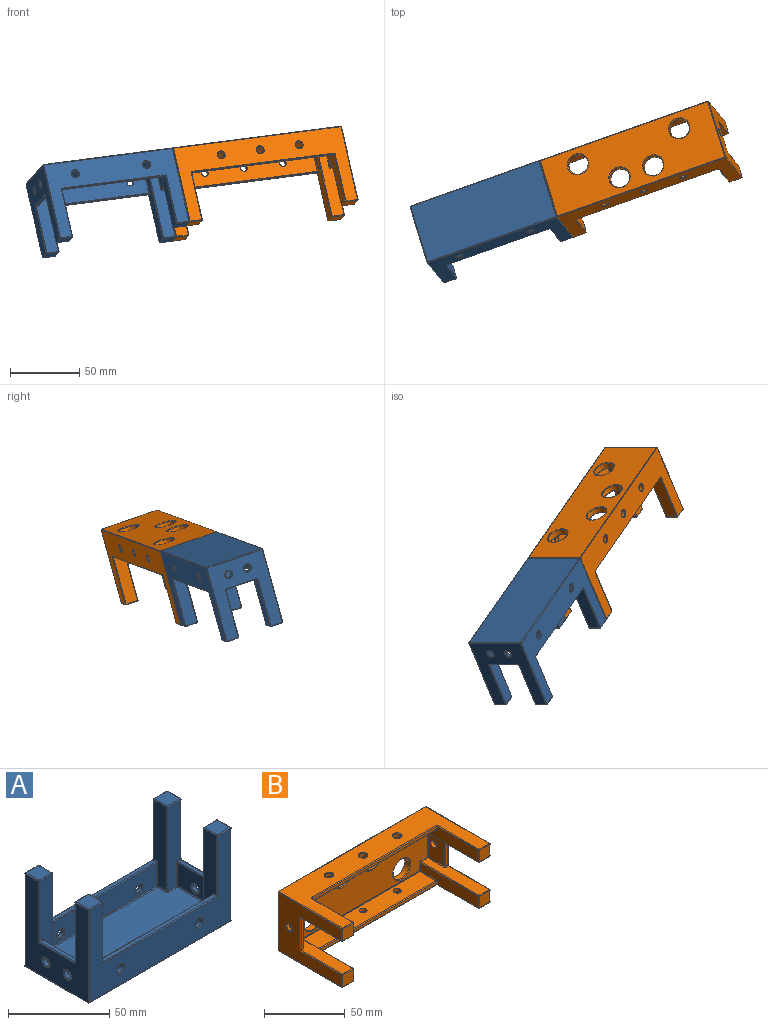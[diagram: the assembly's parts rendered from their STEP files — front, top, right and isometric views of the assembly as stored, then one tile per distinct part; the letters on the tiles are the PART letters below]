
ASSEMBLY  parts=2 mates=1
PART A: 165 faces, bbox 100x45x56.8 mm
  f0: plane 55.8x44mm, normal (1,0,0), area 1470.6mm2, adj f43,f115,f116,f127,f138,f139,f146,f151
  f1: plane 99x55.8mm, normal (0,1,0), area 2487.3mm2, adj f33,f35,f111,f134,f135,f143,f149,f150
  f2: plane 79x14mm, normal (0,-1,0), area 1049.5mm2, adj f34,f36,f108,f109,f131,f132
  f3: plane 99x55.8mm, normal (0,-1,0), area 2487.3mm2, adj f37,f38,f68,f77,f78,f86,f94,f95
  f4: plane 79x14mm, normal (0,1,0), area 1066.7mm2, adj f29,f30,f48,f54,f61,f62
  f5: plane 55.8x44mm, normal (-1,0,0), area 1442.3mm2, adj f39,f41,f66,f73,f74,f83,f92,f93
  f6: plane 24x14mm, normal (1,0,0), area 279.5mm2, adj f40,f42,f45,f55,f56,f57
  f7: plane 9x9mm, normal (0,0,1), area 81mm2, adj f96,f97,f114,f115
  f8: plane 9x9mm, normal (0,0,1), area 81mm2, adj f91,f110,f111,f112
  f9: plane 9x9mm, normal (0,0,1), area 81mm2, adj f153,f158,f161,f164
  f10: plane 9x9mm, normal (0,0,1), area 81mm2, adj f75,f76,f93,f94
  f11: plane 99x44mm, normal (0,0,-1), area 4356mm2, adj f136,f137,f150,f151
  f12: plane 50.8x9mm, normal (0,-1,0), area 412.4mm2, adj f56,f65,f71,f72,f90,f91,f92
  f13: plane 50.8x9mm, normal (0,1,0), area 412.4mm2, adj f45,f46,f51,f58,f59,f74,f75
  f14: plane 50.8x9mm, normal (1,0,0), area 412.4mm2, adj f47,f48,f53,f59,f60,f76,f77
  f15: plane 50.8x9mm, normal (-1,0,0), area 412.4mm2, adj f62,f69,f70,f79,f80,f95,f96
  f16: plane 50.8x9mm, normal (0,1,0), area 412.4mm2, adj f80,f88,f97,f98,f106,f116,f117
  f17: plane 24x14mm, normal (-1,0,0), area 307.7mm2, adj f44,f98,f107,f118,f119
  f18: plane 50.8x9mm, normal (0,-1,0), area 412.4mm2, adj f119,f128,f129,f140,f147,f152,f153
  f19: plane 50.8x9mm, normal (-1,0,0), area 412.4mm2, adj f130,f131,f142,f147,f148,f158,f159
  f20: plane 50.8x9mm, normal (1,0,0), area 412.4mm2, adj f89,f90,f109,f110,f122,f133,f134
  f21: plane 93x38mm, normal (0,0,1), area 3338.9mm2, adj f46,f47,f52,f54,f55,f70,f71,f81
  f22: plane 24x2mm, normal (0,0,1), area 48mm2, adj f117,f118,f139,f140
  f23: plane 79x2mm, normal (0,0,1), area 158mm2, adj f60,f61,f78,f79
  f24: plane 24x2mm, normal (0,0,1), area 48mm2, adj f57,f58,f72,f73
  f25: plane 79x2mm, normal (0,0,1), area 158mm2, adj f132,f133,f148,f149
  f26: cylinder r=2.5mm len=5mm, axis (1,0,0), area 31.4mm2, adj f43,f44
  f27: cylinder r=2.5mm len=5mm, axis (-1,0,0), area 31.4mm2, adj f39,f40
  f28: cylinder r=2.5mm len=5mm, axis (-1,0,0), area 31.4mm2, adj f41,f42
  f29: cylinder r=2.5mm len=5mm, axis (0,-1,0), area 39.3mm2, adj f4,f37
  f30: cylinder r=2.5mm len=5mm, axis (0,-1,0), area 39.3mm2, adj f4,f38
  f31: cylinder r=2.5mm len=5mm, axis (0,1,0), area 31.4mm2, adj f33,f34
  f32: cylinder r=2.5mm len=5mm, axis (0,1,0), area 31.4mm2, adj f35,f36
  f33: torus R=3mm, axis (0,1,0), area 13.2mm2, adj f1,f31
  f34: torus R=3mm, axis (0,-1,0), area 13.2mm2, adj f2,f31
  f35: torus R=3mm, axis (0,1,0), area 13.2mm2, adj f1,f32
  f36: torus R=3mm, axis (0,-1,0), area 13.2mm2, adj f2,f32
  f37: torus R=3mm, axis (0,1,0), area 13.2mm2, adj f3,f29
  f38: torus R=3mm, axis (0,1,0), area 13.2mm2, adj f3,f30
  f39: torus R=3mm, axis (1,0,0), area 13.2mm2, adj f5,f27
  f40: torus R=3mm, axis (-1,0,0), area 13.2mm2, adj f6,f27
  f41: torus R=3mm, axis (1,0,0), area 13.2mm2, adj f5,f28
  f42: torus R=3mm, axis (-1,0,0), area 13.2mm2, adj f6,f28
  f43: torus R=3mm, axis (1,0,0), area 13.2mm2, adj f0,f26
  f44: torus R=3mm, axis (-1,0,0), area 13.2mm2, adj f17,f26
  f45: cylinder r=0.5mm len=14mm, axis (0,0,-1), area 11mm2, adj f6,f13,f50,f51
  f46: cylinder r=0.5mm len=6mm, axis (1,0,0), area 4.7mm2, adj f13,f21,f50,f52
  f47: cylinder r=0.5mm len=6mm, axis (0,-1,0), area 4.7mm2, adj f14,f21,f49,f52
  f48: cylinder r=0.5mm len=14mm, axis (0,0,1), area 11mm2, adj f4,f14,f49,f53
  f49: sphere r=0.5mm, area 0.4mm2, adj f47,f48,f54
  f50: sphere r=0.5mm, area 0.4mm2, adj f45,f46,f55
  f51: torus R=1mm, axis (0,-1,0), area 0.8mm2, adj f13,f45,f57,f58
  f52: torus R=1mm, axis (0,0,1), area 0.8mm2, adj f21,f46,f47,f59
  f53: torus R=1mm, axis (1,0,0), area 0.8mm2, adj f14,f48,f60,f61
  f54: cylinder r=0.5mm len=79mm, axis (1,0,0), area 62mm2, adj f4,f21,f49,f63
  f55: cylinder r=0.5mm len=24mm, axis (0,-1,0), area 18.8mm2, adj f6,f21,f50,f64
  f56: cylinder r=0.5mm len=14mm, axis (0,0,1), area 11mm2, adj f6,f12,f64,f65
  f57: cylinder r=0.5mm len=24mm, axis (0,1,0), area 18.8mm2, adj f6,f24,f51,f65
  f58: cylinder r=0.5mm len=2mm, axis (1,0,0), area 1.6mm2, adj f13,f24,f51,f66
  f59: cylinder r=0.5mm len=50.8mm, axis (0,0,-1), area 39.9mm2, adj f13,f14,f52,f67
  f60: cylinder r=0.5mm len=2mm, axis (0,1,0), area 1.6mm2, adj f14,f23,f53,f68
  f61: cylinder r=0.5mm len=79mm, axis (-1,0,0), area 62mm2, adj f4,f23,f53,f69
  f62: cylinder r=0.5mm len=14mm, axis (0,0,-1), area 11mm2, adj f4,f15,f63,f69
  f63: sphere r=0.5mm, area 0.4mm2, adj f54,f62,f70
  f64: sphere r=0.5mm, area 0.4mm2, adj f55,f56,f71
  f65: torus R=1mm, axis (0,-1,0), area 0.8mm2, adj f12,f56,f57,f72
  f66: torus R=1mm, axis (1,0,0), area 0.8mm2, adj f5,f58,f73,f74
  f67: sphere r=0.5mm, area 0.4mm2, adj f59,f75,f76
  f68: torus R=1mm, axis (0,1,0), area 0.8mm2, adj f3,f60,f77,f78
  f69: torus R=1mm, axis (1,0,0), area 0.8mm2, adj f15,f61,f62,f79
  f70: cylinder r=0.5mm len=6mm, axis (0,1,0), area 4.7mm2, adj f15,f21,f63,f81
  f71: cylinder r=0.5mm len=6mm, axis (-1,0,0), area 4.7mm2, adj f12,f21,f64,f82
  f72: cylinder r=0.5mm len=2mm, axis (-1,0,0), area 1.6mm2, adj f12,f24,f65,f83
  f73: cylinder r=0.5mm len=24mm, axis (0,1,0), area 18.8mm2, adj f5,f24,f66,f83
  f74: cylinder r=0.5mm len=35.8mm, axis (0,0,1), area 28.1mm2, adj f5,f13,f66,f84
  f75: cylinder r=0.5mm len=9mm, axis (-1,0,0), area 7.1mm2, adj f10,f13,f67,f84
  f76: cylinder r=0.5mm len=9mm, axis (0,1,0), area 7.1mm2, adj f10,f14,f67,f85
  f77: cylinder r=0.5mm len=35.8mm, axis (0,0,-1), area 28.1mm2, adj f3,f14,f68,f85
  f78: cylinder r=0.5mm len=79mm, axis (-1,0,0), area 62mm2, adj f3,f23,f68,f86
  f79: cylinder r=0.5mm len=2mm, axis (0,-1,0), area 1.6mm2, adj f15,f23,f69,f86
  f80: cylinder r=0.5mm len=50.8mm, axis (0,0,-1), area 39.9mm2, adj f15,f16,f81,f87
  f81: torus R=1mm, axis (0,0,1), area 0.8mm2, adj f21,f70,f80,f88
  f82: torus R=1mm, axis (0,0,1), area 0.8mm2, adj f21,f71,f89,f90
  f83: torus R=1mm, axis (1,0,0), area 0.8mm2, adj f5,f72,f73,f92
  f84: sphere r=0.5mm, area 0.4mm2, adj f74,f75,f93
  f85: sphere r=0.5mm, area 0.4mm2, adj f76,f77,f94
  f86: torus R=1mm, axis (0,1,0), area 0.8mm2, adj f3,f78,f79,f95
  f87: sphere r=0.5mm, area 0.4mm2, adj f80,f96,f97
  f88: cylinder r=0.5mm len=6mm, axis (1,0,0), area 4.7mm2, adj f16,f21,f81,f99
  f89: cylinder r=0.5mm len=6mm, axis (0,-1,0), area 4.7mm2, adj f20,f21,f82,f100
  f90: cylinder r=0.5mm len=50.8mm, axis (0,0,-1), area 39.9mm2, adj f12,f20,f82,f101
  f91: cylinder r=0.5mm len=9mm, axis (1,0,0), area 7.1mm2, adj f8,f12,f101,f102
  f92: cylinder r=0.5mm len=35.8mm, axis (0,0,-1), area 28.1mm2, adj f5,f12,f83,f102
  f93: cylinder r=0.5mm len=9mm, axis (0,1,0), area 7.1mm2, adj f5,f10,f84,f103
  f94: cylinder r=0.5mm len=9mm, axis (-1,0,0), area 7.1mm2, adj f3,f10,f85,f103
  f95: cylinder r=0.5mm len=35.8mm, axis (0,0,1), area 28.1mm2, adj f3,f15,f86,f104
  f96: cylinder r=0.5mm len=9mm, axis (0,-1,0), area 7.1mm2, adj f7,f15,f87,f104
  f97: cylinder r=0.5mm len=9mm, axis (-1,0,0), area 7.1mm2, adj f7,f16,f87,f105
  f98: cylinder r=0.5mm len=14mm, axis (0,0,-1), area 11mm2, adj f16,f17,f99,f106
  f99: sphere r=0.5mm, area 0.4mm2, adj f88,f98,f107
  f100: sphere r=0.5mm, area 0.4mm2, adj f89,f108,f109
  f101: sphere r=0.5mm, area 0.4mm2, adj f90,f91,f110
  f102: sphere r=0.5mm, area 0.4mm2, adj f91,f92,f112
  f103: sphere r=0.5mm, area 0.4mm2, adj f93,f94,f113
  f104: sphere r=0.5mm, area 0.4mm2, adj f95,f96,f114
  f105: sphere r=0.5mm, area 0.4mm2, adj f97,f115,f116
  f106: torus R=1mm, axis (0,1,0), area 0.8mm2, adj f16,f98,f117,f118
  f107: cylinder r=0.5mm len=24mm, axis (0,1,0), area 18.8mm2, adj f17,f21,f99,f120
  f108: cylinder r=0.5mm len=79mm, axis (-1,0,0), area 62mm2, adj f2,f21,f100,f121
  f109: cylinder r=0.5mm len=14mm, axis (0,0,1), area 11mm2, adj f2,f20,f100,f122
  f110: cylinder r=0.5mm len=9mm, axis (0,1,0), area 7.1mm2, adj f8,f20,f101,f123
  f111: cylinder r=0.5mm len=9mm, axis (1,0,0), area 7.1mm2, adj f1,f8,f123,f124
  f112: cylinder r=0.5mm len=9mm, axis (0,1,0), area 7.1mm2, adj f5,f8,f102,f124
  f113: cylinder r=0.5mm len=55.8mm, axis (0,0,-1), area 43.8mm2, adj f3,f5,f103,f125
  f114: cylinder r=0.5mm len=9mm, axis (-1,0,0), area 7.1mm2, adj f3,f7,f104,f126
  f115: cylinder r=0.5mm len=9mm, axis (0,-1,0), area 7.1mm2, adj f0,f7,f105,f126
  f116: cylinder r=0.5mm len=35.8mm, axis (0,0,1), area 28.1mm2, adj f0,f16,f105,f127
  f117: cylinder r=0.5mm len=2mm, axis (1,0,0), area 1.6mm2, adj f16,f22,f106,f127
  f118: cylinder r=0.5mm len=24mm, axis (0,-1,0), area 18.8mm2, adj f17,f22,f106,f128
  f119: cylinder r=0.5mm len=14mm, axis (0,0,1), area 11mm2, adj f17,f18,f120,f128
  f120: sphere r=0.5mm, area 0.4mm2, adj f107,f119,f129
  f121: sphere r=0.5mm, area 0.4mm2, adj f108,f130,f131
  f122: torus R=1mm, axis (-1,0,0), area 0.8mm2, adj f20,f109,f132,f133
  f123: sphere r=0.5mm, area 0.4mm2, adj f110,f111,f134
  f124: sphere r=0.5mm, area 0.4mm2, adj f111,f112,f135
  f125: sphere r=0.5mm, area 0.4mm2, adj f113,f136,f137
  f126: sphere r=0.5mm, area 0.4mm2, adj f114,f115,f138
  f127: torus R=1mm, axis (1,0,0), area 0.8mm2, adj f0,f116,f117,f139
  f128: torus R=1mm, axis (0,1,0), area 0.8mm2, adj f18,f118,f119,f140
  f129: cylinder r=0.5mm len=6mm, axis (-1,0,0), area 4.7mm2, adj f18,f21,f120,f141
  f130: cylinder r=0.5mm len=6mm, axis (0,1,0), area 4.7mm2, adj f19,f21,f121,f141
  f131: cylinder r=0.5mm len=14mm, axis (0,0,-1), area 11mm2, adj f2,f19,f121,f142
  f132: cylinder r=0.5mm len=79mm, axis (1,0,0), area 62mm2, adj f2,f25,f122,f142
  f133: cylinder r=0.5mm len=2mm, axis (0,1,0), area 1.6mm2, adj f20,f25,f122,f143
  f134: cylinder r=0.5mm len=35.8mm, axis (0,0,-1), area 28.1mm2, adj f1,f20,f123,f143
  f135: cylinder r=0.5mm len=55.8mm, axis (0,0,1), area 43.8mm2, adj f1,f5,f124,f144
  f136: cylinder r=0.5mm len=44mm, axis (0,-1,0), area 34.6mm2, adj f5,f11,f125,f144
  f137: cylinder r=0.5mm len=99mm, axis (1,0,0), area 77.8mm2, adj f3,f11,f125,f145
  f138: cylinder r=0.5mm len=55.8mm, axis (0,0,1), area 43.8mm2, adj f0,f3,f126,f145
  f139: cylinder r=0.5mm len=24mm, axis (0,-1,0), area 18.8mm2, adj f0,f22,f127,f146
  f140: cylinder r=0.5mm len=2mm, axis (-1,0,0), area 1.6mm2, adj f18,f22,f128,f146
  f141: torus R=1mm, axis (0,0,1), area 0.8mm2, adj f21,f129,f130,f147
  f142: torus R=1mm, axis (-1,0,0), area 0.8mm2, adj f19,f131,f132,f148
  f143: torus R=1mm, axis (0,1,0), area 0.8mm2, adj f1,f133,f134,f149
  f144: sphere r=0.5mm, area 0.4mm2, adj f135,f136,f150
  f145: sphere r=0.5mm, area 0.4mm2, adj f137,f138,f151
  f146: torus R=1mm, axis (1,0,0), area 0.8mm2, adj f0,f139,f140,f152
  f147: cylinder r=0.5mm len=50.8mm, axis (0,0,-1), area 39.9mm2, adj f18,f19,f141,f154
  f148: cylinder r=0.5mm len=2mm, axis (0,-1,0), area 1.6mm2, adj f19,f25,f142,f155
  f149: cylinder r=0.5mm len=79mm, axis (1,0,0), area 62mm2, adj f1,f25,f143,f155
  f150: cylinder r=0.5mm len=99mm, axis (-1,0,0), area 77.8mm2, adj f1,f11,f144,f156
  f151: cylinder r=0.5mm len=44mm, axis (0,1,0), area 34.6mm2, adj f0,f11,f145,f156
  f152: cylinder r=0.5mm len=35.8mm, axis (0,0,-1), area 28.1mm2, adj f0,f18,f146,f157
  f153: cylinder r=0.5mm len=9mm, axis (1,0,0), area 7.1mm2, adj f9,f18,f154,f157
  f154: sphere r=0.5mm, area 0.4mm2, adj f147,f153,f158
  f155: torus R=1mm, axis (0,1,0), area 0.8mm2, adj f1,f148,f149,f159
  f156: sphere r=0.5mm, area 0.4mm2, adj f150,f151,f160
  f157: sphere r=0.5mm, area 0.4mm2, adj f152,f153,f161
  f158: cylinder r=0.5mm len=9mm, axis (0,-1,0), area 7.1mm2, adj f9,f19,f154,f162
  f159: cylinder r=0.5mm len=35.8mm, axis (0,0,1), area 28.1mm2, adj f1,f19,f155,f162
  f160: cylinder r=0.5mm len=55.8mm, axis (0,0,-1), area 43.8mm2, adj f0,f1,f156,f163
  f161: cylinder r=0.5mm len=9mm, axis (0,-1,0), area 7.1mm2, adj f0,f9,f157,f163
  f162: sphere r=0.5mm, area 0.4mm2, adj f158,f159,f164
  f163: sphere r=0.5mm, area 0.4mm2, adj f160,f161,f164
  f164: cylinder r=0.5mm len=9mm, axis (1,0,0), area 7.1mm2, adj f1,f9,f162,f163
PART B: 165 faces, bbox 130x56.8x45 mm
  f0: plane 50.8x9mm, normal (1,0,0), area 412.4mm2, adj f63,f64,f74,f85,f86,f104,f105
  f1: plane 50.8x9mm, normal (0,0,1), area 412.4mm2, adj f45,f46,f58,f59,f71,f82,f83
  f2: plane 129x55.8mm, normal (0,0,-1), area 3029mm2, adj f38,f39,f43,f49,f50,f54,f64,f65
  f3: plane 50.8x9mm, normal (0,0,1), area 421mm2, adj f22,f23,f87,f88,f105,f119,f164
  f4: plane 123x38mm, normal (0,-1,0), area 3694.6mm2, adj f60,f72,f83,f84,f103,f104,f113,f118
  f5: plane 50.8x9mm, normal (-1,0,0), area 412.4mm2, adj f110,f117,f123,f129,f134,f135,f139
  f6: plane 55.8x44mm, normal (-1,0,0), area 1470.1mm2, adj f66,f67,f88,f89,f98,f106,f107,f108
  f7: plane 109x2mm, normal (0,-1,0), area 218mm2, adj f133,f134,f142,f143
  f8: plane 109x2mm, normal (0,-1,0), area 218mm2, adj f48,f49,f62,f63
  f9: plane 9x9mm, normal (0,-1,0), area 81mm2, adj f65,f66,f86,f87
  f10: plane 9x9mm, normal (0,-1,0), area 81mm2, adj f39,f40,f46,f47
  f11: plane 55.8x44mm, normal (1,0,0), area 1470.6mm2, adj f40,f45,f50,f51,f57,f69,f70,f79
  f12: plane 9x9mm, normal (0,-1,0), area 81mm2, adj f107,f120,f121,f122
  f13: plane 129x55.8mm, normal (0,0,1), area 3029mm2, adj f90,f91,f108,f109,f122,f123,f128,f132
  f14: plane 9x9mm, normal (0,-1,0), area 81mm2, adj f92,f101,f109,f110
  f15: plane 129x44mm, normal (0,1,0), area 4891.7mm2, adj f68,f69,f89,f90,f156,f158,f160,f162
  f16: plane 50.8x9mm, normal (1,0,0), area 412.4mm2, adj f121,f131,f132,f141,f142,f145,f146
  f17: plane 50.8x9mm, normal (-1,0,0), area 412.4mm2, adj f38,f47,f48,f53,f59,f60,f61
  f18: plane 50.8x9mm, normal (0,0,-1), area 412.4mm2, adj f79,f80,f94,f101,f102,f117,f118
  f19: plane 50.8x9mm, normal (0,0,-1), area 421mm2, adj f22,f23,f106,f120,f130,f131,f164
  f20: plane 109x14mm, normal (0,0,-1), area 1467.1mm2, adj f30,f31,f32,f135,f140,f143,f146
  f21: plane 109x14mm, normal (0,0,1), area 1467.1mm2, adj f34,f35,f36,f61,f62,f84,f85
  f22: plane 25x14mm, normal (1,0,0), area 321.7mm2, adj f3,f19,f125,f148,f164
  f23: plane 25x2mm, normal (0,-1,0), area 50mm2, adj f3,f19,f98,f164
  f24: plane 24x14mm, normal (-1,0,0), area 316.4mm2, adj f33,f81,f82,f102,f103
  f25: plane 24x2mm, normal (0,-1,0), area 48mm2, adj f57,f58,f80,f81
  f26: cylinder r=7.4mm len=14.8mm, axis (0,1,0), area 186mm2, adj f156,f157
  f27: cylinder r=7.4mm len=14.8mm, axis (0,1,0), area 186mm2, adj f158,f159
  f28: cylinder r=7.4mm len=14.8mm, axis (0,1,0), area 186mm2, adj f160,f161
  f29: cylinder r=7.4mm len=14.8mm, axis (0,1,0), area 186mm2, adj f162,f163
  f30: cylinder r=2.5mm len=5mm, axis (0,0,1), area 39.3mm2, adj f20,f153
  f31: cylinder r=2.5mm len=5mm, axis (0,0,1), area 39.3mm2, adj f20,f154
  f32: cylinder r=2.5mm len=5mm, axis (0,0,1), area 39.3mm2, adj f20,f155
  f33: cylinder r=2.5mm len=5mm, axis (1,0,0), area 39.3mm2, adj f24,f152
  f34: cylinder r=2.5mm len=5mm, axis (0,0,-1), area 39.3mm2, adj f21,f149
  f35: cylinder r=2.5mm len=5mm, axis (0,0,-1), area 39.3mm2, adj f21,f150
  f36: cylinder r=2.5mm len=5mm, axis (0,0,-1), area 39.3mm2, adj f21,f151
  f37: cylinder r=2.5mm len=5mm, axis (-1,0,0), area 31.4mm2, adj f147,f148
  f38: cylinder r=0.5mm len=35.8mm, axis (0,-1,0), area 28.1mm2, adj f2,f17,f42,f43
  f39: cylinder r=0.5mm len=9mm, axis (-1,0,0), area 7.1mm2, adj f2,f10,f42,f44
  f40: cylinder r=0.5mm len=9mm, axis (0,0,-1), area 7.1mm2, adj f10,f11,f41,f44
  f41: sphere r=0.5mm, area 0.4mm2, adj f40,f45,f46
  f42: sphere r=0.5mm, area 0.4mm2, adj f38,f39,f47
  f43: torus R=1mm, axis (0,0,-1), area 0.8mm2, adj f2,f38,f48,f49
  f44: sphere r=0.5mm, area 0.4mm2, adj f39,f40,f50
  f45: cylinder r=0.5mm len=35.8mm, axis (0,-1,0), area 28.1mm2, adj f1,f11,f41,f51
  f46: cylinder r=0.5mm len=9mm, axis (1,0,0), area 7.1mm2, adj f1,f10,f41,f52
  f47: cylinder r=0.5mm len=9mm, axis (0,0,1), area 7.1mm2, adj f10,f17,f42,f52
  f48: cylinder r=0.5mm len=2mm, axis (0,0,-1), area 1.6mm2, adj f8,f17,f43,f53
  f49: cylinder r=0.5mm len=109mm, axis (1,0,0), area 85.6mm2, adj f2,f8,f43,f54
  f50: cylinder r=0.5mm len=55.8mm, axis (0,-1,0), area 43.8mm2, adj f2,f11,f44,f56
  f51: torus R=1mm, axis (-1,0,0), area 0.8mm2, adj f11,f45,f57,f58
  f52: sphere r=0.5mm, area 0.4mm2, adj f46,f47,f59
  f53: torus R=1mm, axis (-1,0,0), area 0.8mm2, adj f17,f48,f61,f62
  f54: torus R=1mm, axis (0,0,-1), area 0.8mm2, adj f2,f49,f63,f64
  f55: sphere r=0.5mm, area 0.4mm2, adj f65,f66,f67
  f56: sphere r=0.5mm, area 0.4mm2, adj f50,f68,f69
  f57: cylinder r=0.5mm len=24mm, axis (0,0,1), area 18.8mm2, adj f11,f25,f51,f70
  f58: cylinder r=0.5mm len=2mm, axis (-1,0,0), area 1.6mm2, adj f1,f25,f51,f71
  f59: cylinder r=0.5mm len=50.8mm, axis (0,1,0), area 39.9mm2, adj f1,f17,f52,f72
  f60: cylinder r=0.5mm len=6mm, axis (0,0,-1), area 4.7mm2, adj f4,f17,f72,f73
  f61: cylinder r=0.5mm len=14mm, axis (0,1,0), area 11mm2, adj f17,f21,f53,f73
  f62: cylinder r=0.5mm len=109mm, axis (-1,0,0), area 85.6mm2, adj f8,f21,f53,f74
  f63: cylinder r=0.5mm len=2mm, axis (0,0,-1), area 1.6mm2, adj f0,f8,f54,f74
  f64: cylinder r=0.5mm len=35.8mm, axis (0,1,0), area 28.1mm2, adj f0,f2,f54,f75
  f65: cylinder r=0.5mm len=9mm, axis (-1,0,0), area 7.1mm2, adj f2,f9,f55,f75
  f66: cylinder r=0.5mm len=9mm, axis (0,0,1), area 7.1mm2, adj f6,f9,f55,f76
  f67: cylinder r=0.5mm len=55.8mm, axis (0,1,0), area 43.8mm2, adj f2,f6,f55,f77
  f68: cylinder r=0.5mm len=129mm, axis (1,0,0), area 101.3mm2, adj f2,f15,f56,f77
  f69: cylinder r=0.5mm len=44mm, axis (0,0,1), area 34.6mm2, adj f11,f15,f56,f78
  f70: torus R=1mm, axis (-1,0,0), area 0.8mm2, adj f11,f57,f79,f80
  f71: torus R=1mm, axis (0,0,-1), area 0.8mm2, adj f1,f58,f81,f82
  f72: torus R=1mm, axis (0,-1,0), area 0.8mm2, adj f4,f59,f60,f83
  f73: sphere r=0.5mm, area 0.4mm2, adj f60,f61,f84
  f74: torus R=1mm, axis (1,0,0), area 0.8mm2, adj f0,f62,f63,f85
  f75: sphere r=0.5mm, area 0.4mm2, adj f64,f65,f86
  f76: sphere r=0.5mm, area 0.4mm2, adj f66,f87,f88
  f77: sphere r=0.5mm, area 0.4mm2, adj f67,f68,f89
  f78: sphere r=0.5mm, area 0.4mm2, adj f69,f90,f91
  f79: cylinder r=0.5mm len=35.8mm, axis (0,1,0), area 28.1mm2, adj f11,f18,f70,f93
  f80: cylinder r=0.5mm len=2mm, axis (1,0,0), area 1.6mm2, adj f18,f25,f70,f94
  f81: cylinder r=0.5mm len=24mm, axis (0,0,1), area 18.8mm2, adj f24,f25,f71,f94
  f82: cylinder r=0.5mm len=14mm, axis (0,-1,0), area 11mm2, adj f1,f24,f71,f95
  f83: cylinder r=0.5mm len=6mm, axis (-1,0,0), area 4.7mm2, adj f1,f4,f72,f95
  f84: cylinder r=0.5mm len=109mm, axis (1,0,0), area 85.6mm2, adj f4,f21,f73,f96
  f85: cylinder r=0.5mm len=14mm, axis (0,1,0), area 11mm2, adj f0,f21,f74,f96
  f86: cylinder r=0.5mm len=9mm, axis (0,0,1), area 7.1mm2, adj f0,f9,f75,f97
  f87: cylinder r=0.5mm len=9mm, axis (1,0,0), area 7.1mm2, adj f3,f9,f76,f97
  f88: cylinder r=0.5mm len=36.8mm, axis (0,1,0), area 28.7mm2, adj f3,f6,f76,f98
  f89: cylinder r=0.5mm len=44mm, axis (0,0,-1), area 34.6mm2, adj f6,f15,f77,f99
  f90: cylinder r=0.5mm len=129mm, axis (-1,0,0), area 101.3mm2, adj f13,f15,f78,f99
  f91: cylinder r=0.5mm len=55.8mm, axis (0,1,0), area 43.8mm2, adj f11,f13,f78,f100
  f92: cylinder r=0.5mm len=9mm, axis (0,0,-1), area 7.1mm2, adj f11,f14,f93,f100
  f93: sphere r=0.5mm, area 0.4mm2, adj f79,f92,f101
  f94: torus R=1mm, axis (0,0,-1), area 0.8mm2, adj f18,f80,f81,f102
  f95: sphere r=0.5mm, area 0.4mm2, adj f82,f83,f103
  f96: sphere r=0.5mm, area 0.4mm2, adj f84,f85,f104
  f97: sphere r=0.5mm, area 0.4mm2, adj f86,f87,f105
  f98: cylinder r=0.5mm len=26mm, axis (0,0,-1), area 19.9mm2, adj f6,f23,f88,f106
  f99: sphere r=0.5mm, area 0.4mm2, adj f89,f90,f108
  f100: sphere r=0.5mm, area 0.4mm2, adj f91,f92,f109
  f101: cylinder r=0.5mm len=9mm, axis (-1,0,0), area 7.1mm2, adj f14,f18,f93,f111
  f102: cylinder r=0.5mm len=14mm, axis (0,1,0), area 11mm2, adj f18,f24,f94,f112
  f103: cylinder r=0.5mm len=24mm, axis (0,0,-1), area 18.8mm2, adj f4,f24,f95,f112
  f104: cylinder r=0.5mm len=6mm, axis (0,0,-1), area 4.7mm2, adj f0,f4,f96,f113
  f105: cylinder r=0.5mm len=50.8mm, axis (0,-1,0), area 39.9mm2, adj f0,f3,f97,f113
  f106: cylinder r=0.5mm len=36.8mm, axis (0,-1,0), area 28.7mm2, adj f6,f19,f98,f114
  f107: cylinder r=0.5mm len=9mm, axis (0,0,1), area 7.1mm2, adj f6,f12,f114,f115
  f108: cylinder r=0.5mm len=55.8mm, axis (0,-1,0), area 43.8mm2, adj f6,f13,f99,f115
  f109: cylinder r=0.5mm len=9mm, axis (1,0,0), area 7.1mm2, adj f13,f14,f100,f116
  f110: cylinder r=0.5mm len=9mm, axis (0,0,1), area 7.1mm2, adj f5,f14,f111,f116
  f111: sphere r=0.5mm, area 0.4mm2, adj f101,f110,f117
  f112: sphere r=0.5mm, area 0.4mm2, adj f102,f103,f118
  f113: torus R=1mm, axis (0,-1,0), area 0.8mm2, adj f4,f104,f105,f119
  f114: sphere r=0.5mm, area 0.4mm2, adj f106,f107,f120
  f115: sphere r=0.5mm, area 0.4mm2, adj f107,f108,f122
  f116: sphere r=0.5mm, area 0.4mm2, adj f109,f110,f123
  f117: cylinder r=0.5mm len=50.8mm, axis (0,-1,0), area 39.9mm2, adj f5,f18,f111,f124
  f118: cylinder r=0.5mm len=6mm, axis (1,0,0), area 4.7mm2, adj f4,f18,f112,f124
  f119: cylinder r=0.5mm len=6.5mm, axis (-1,0,0), area 5mm2, adj f3,f4,f113,f125
  f120: cylinder r=0.5mm len=9mm, axis (-1,0,0), area 7.1mm2, adj f12,f19,f114,f126
  f121: cylinder r=0.5mm len=9mm, axis (0,0,1), area 7.1mm2, adj f12,f16,f126,f127
  f122: cylinder r=0.5mm len=9mm, axis (1,0,0), area 7.1mm2, adj f12,f13,f115,f127
  f123: cylinder r=0.5mm len=35.8mm, axis (0,1,0), area 28.1mm2, adj f5,f13,f116,f128
  f124: torus R=1mm, axis (0,-1,0), area 0.8mm2, adj f4,f117,f118,f129
  f125: cylinder r=0.5mm len=25mm, axis (0,0,1), area 19.3mm2, adj f4,f22,f119,f130
  f126: sphere r=0.5mm, area 0.4mm2, adj f120,f121,f131
  f127: sphere r=0.5mm, area 0.4mm2, adj f121,f122,f132
  f128: torus R=1mm, axis (0,0,-1), area 0.8mm2, adj f13,f123,f133,f134
  f129: cylinder r=0.5mm len=6mm, axis (0,0,-1), area 4.7mm2, adj f4,f5,f124,f136
  f130: cylinder r=0.5mm len=6.5mm, axis (1,0,0), area 5mm2, adj f4,f19,f125,f137
  f131: cylinder r=0.5mm len=50.8mm, axis (0,1,0), area 39.9mm2, adj f16,f19,f126,f137
  f132: cylinder r=0.5mm len=35.8mm, axis (0,-1,0), area 28.1mm2, adj f13,f16,f127,f138
  f133: cylinder r=0.5mm len=109mm, axis (-1,0,0), area 85.6mm2, adj f7,f13,f128,f138
  f134: cylinder r=0.5mm len=2mm, axis (0,0,-1), area 1.6mm2, adj f5,f7,f128,f139
  f135: cylinder r=0.5mm len=14mm, axis (0,1,0), area 11mm2, adj f5,f20,f136,f139
  f136: sphere r=0.5mm, area 0.4mm2, adj f129,f135,f140
  f137: torus R=1mm, axis (0,-1,0), area 0.8mm2, adj f4,f130,f131,f141
  f138: torus R=1mm, axis (0,0,-1), area 0.8mm2, adj f13,f132,f133,f142
  f139: torus R=1mm, axis (-1,0,0), area 0.8mm2, adj f5,f134,f135,f143
  f140: cylinder r=0.5mm len=109mm, axis (-1,0,0), area 85.6mm2, adj f4,f20,f136,f144
  f141: cylinder r=0.5mm len=6mm, axis (0,0,-1), area 4.7mm2, adj f4,f16,f137,f144
  f142: cylinder r=0.5mm len=2mm, axis (0,0,-1), area 1.6mm2, adj f7,f16,f138,f145
  f143: cylinder r=0.5mm len=109mm, axis (1,0,0), area 85.6mm2, adj f7,f20,f139,f145
  f144: sphere r=0.5mm, area 0.4mm2, adj f140,f141,f146
  f145: torus R=1mm, axis (1,0,0), area 0.8mm2, adj f16,f142,f143,f146
  f146: cylinder r=0.5mm len=14mm, axis (0,1,0), area 11mm2, adj f16,f20,f144,f145
  f147: torus R=3mm, axis (-1,0,0), area 13.2mm2, adj f6,f37
  f148: torus R=3mm, axis (1,0,0), area 13.2mm2, adj f22,f37
  f149: torus R=3mm, axis (0,0,-1), area 13.2mm2, adj f2,f34
  f150: torus R=3mm, axis (0,0,-1), area 13.2mm2, adj f2,f35
  f151: torus R=3mm, axis (0,0,-1), area 13.2mm2, adj f2,f36
  f152: torus R=3mm, axis (-1,0,0), area 13.2mm2, adj f11,f33
  f153: torus R=3mm, axis (0,0,-1), area 13.2mm2, adj f13,f30
  f154: torus R=3mm, axis (0,0,-1), area 13.2mm2, adj f13,f31
  f155: torus R=3mm, axis (0,0,-1), area 13.2mm2, adj f13,f32
  f156: torus R=7.9mm, axis (0,-1,0), area 37.4mm2, adj f15,f26
  f157: torus R=7.9mm, axis (0,-1,0), area 37.4mm2, adj f4,f26
  f158: torus R=7.9mm, axis (0,-1,0), area 37.4mm2, adj f15,f27
  f159: torus R=7.9mm, axis (0,-1,0), area 37.4mm2, adj f4,f27
  f160: torus R=7.9mm, axis (0,-1,0), area 37.4mm2, adj f15,f28
  f161: torus R=7.9mm, axis (0,-1,0), area 37.4mm2, adj f4,f28
  f162: torus R=7.9mm, axis (0,-1,0), area 37.4mm2, adj f15,f29
  f163: torus R=7.9mm, axis (0,-1,0), area 37.4mm2, adj f4,f29
  f164: cylinder r=0.5mm len=25mm, axis (0,0,-1), area 19.6mm2, adj f3,f19,f22,f23
PLACE A rot(axis=(0.98,0.16,0.09),163.1deg) t=(-195.75,-44.17,-31.15)mm
PLACE B rot(axis=(0.96,0.08,0.28),75.3deg) t=(-88.1,-6.17,-17.24)mm
MATE fastened A.f0 <-> B.f6  axis (0.94,0.33,0.12) through (-144.14,-33.49,-46.37)mm
